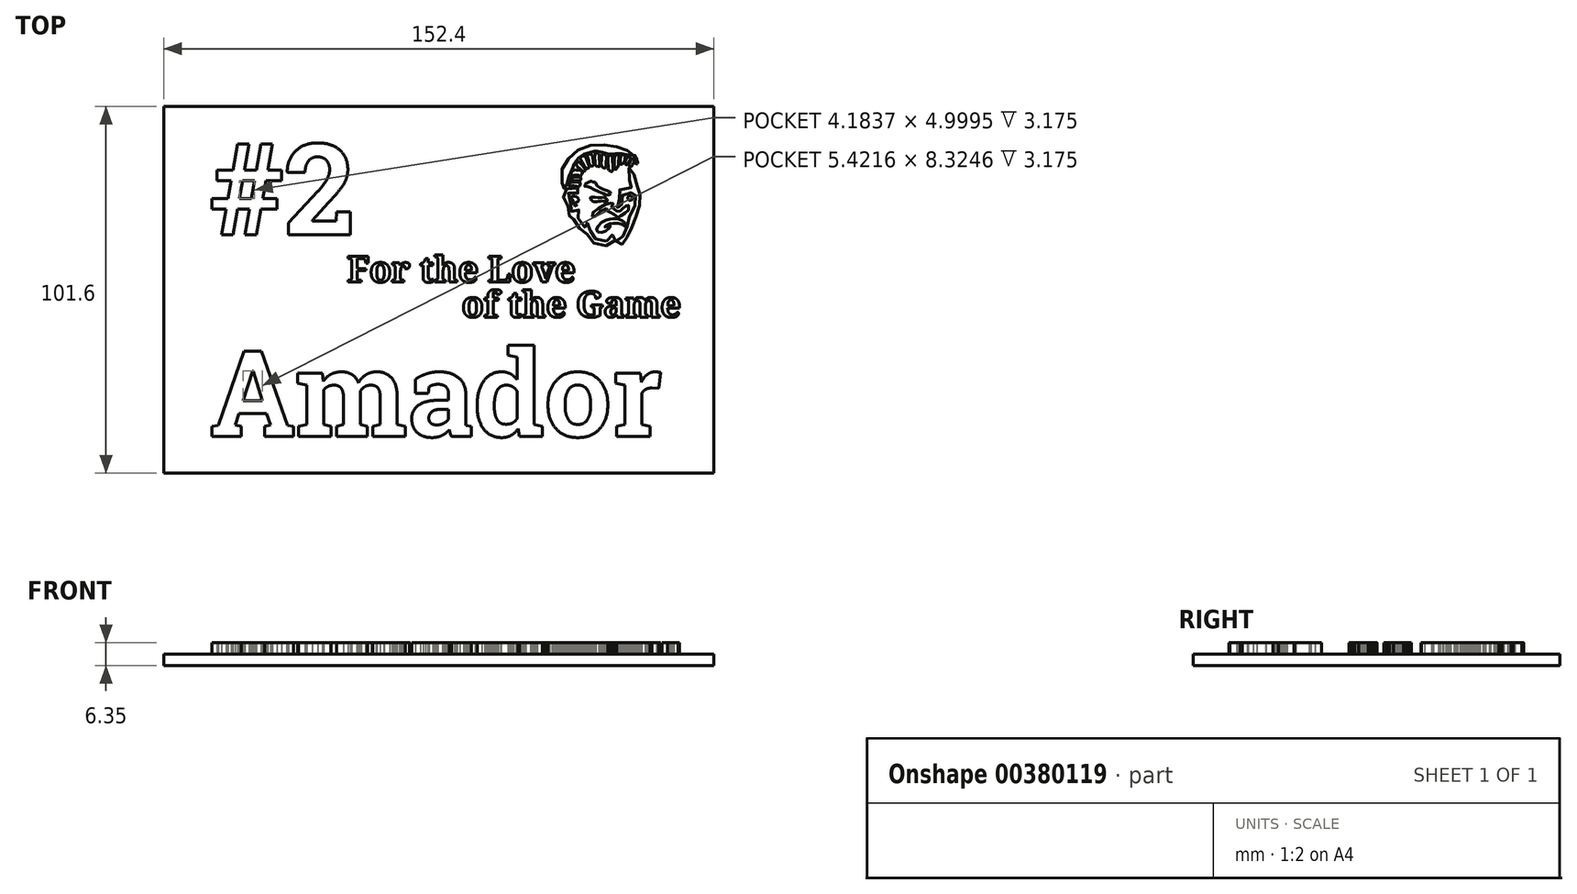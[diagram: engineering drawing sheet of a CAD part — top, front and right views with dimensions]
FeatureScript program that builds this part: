
annotation { "Feature Type Name" : "Feature", "Feature Type Description" : "" }
export const myFeature = defineFeature(function(context is Context, id is Id, definition is map)
    precondition{}
    {
        {
            var Q0;
            Q0=qCreatedBy(makeId("Top.planeOp"),FACE);
            var sketch = newSketch(context, id + "F0", { "sketchPlane" : qUnion([Q0])});
            skLineSegment(sketch, "E0.bottom", {"start": v(-75.13, 26) * mm, "end": v(77.27, 26) * mm});
            skLineSegment(sketch, "E0.top", {"start": v(-75.13, -75.6) * mm, "end": v(77.27, -75.6) * mm});
            skLineSegment(sketch, "E0.left", {"start": v(-75.13, 26) * mm, "end": v(-75.13, -75.6) * mm});
            skLineSegment(sketch, "E0.right", {"start": v(77.27, 26) * mm, "end": v(77.27, -75.6) * mm});
            skSolve(sketch);
        }
        {
            var Q0;
            Q0=makeQuery(id+"F0.imprint","IMPRINT",FACE,{"disambiguationData":[TD([[makeQuery(id+"F0.imprint","IMPRINT",EDGE,{"derivedFrom":sQuery(id+"F0.wireOp",EDGE,"E0.bottom")}),-1.0]])]});
            var sketch = newSketch(context, id + "F1", { "sketchPlane" : qUnion([Q0])});
            skFitSpline(sketch, "E1", {"points": [v(47.57, -11.3) * mm, v(48.35, -11.04) * mm, v(48.7, -10.35) * mm, v(49.04, -9.7) * mm, v(49.57, -9.46) * mm, v(50.02, -9.78) * mm, v(50.06, -10.58) * mm, v(49.74, -11.5) * mm, v(49.1, -12.15) * mm, v(47.63, -12.55) * mm, v(46.12, -12.5) * mm, v(44.61, -12.12) * mm, v(43.38, -11.34) * mm, v(42.6, -10.32) * mm, v(42.24, -9.52) * mm, v(42.15, -9.31) * mm, v(41.34, -8.82) * mm, v(40.33, -8.02) * mm, v(39.44, -7.2) * mm, v(38.67, -6.1) * mm, v(38.42, -5) * mm, v(38.42, -4.22) * mm, v(38.35, -4.2) * mm, v(37.68, -4.39) * mm, v(37.16, -4.27) * mm, v(36.95, -3.72) * mm, v(36.86, -2.5) * mm, v(36.8, -1.48) * mm, v(36.67, -1.07) * mm, v(35.77, 0.2) * mm, v(35.58, 1.07) * mm, v(35.86, 2.13) * mm, v(36.18, 2.7) * mm, v(36.53, 3.12) * mm, v(37.23, 3.22) * mm, v(39.03, 3.4) * mm, v(39.82, 3.34) * mm, v(40.19, 3.09) * mm, v(40.23, 2.45) * mm, v(39.66, 1.98) * mm, v(38.93, 1.9) * mm, v(38.59, 2.03) * mm, v(37.24, 2.03) * mm, v(36.72, 1.65) * mm, v(36.72, 0.85) * mm, v(37.32, -0.2) * mm, v(37.77, -1.18) * mm, v(37.85, -2.09) * mm, v(37.9, -3.1) * mm, v(37.99, -3.1) * mm, v(38.63, -3.1) * mm, v(39.4, -2.76) * mm, v(39.72, -2.59) * mm, v(39.8, -2.7) * mm, v(39.73, -3.22) * mm, v(39.6, -4) * mm, v(39.6, -4.77) * mm, v(40.1, -5.82) * mm, v(41.16, -7.15) * mm, v(41.6, -7.53) * mm, v(41.9, -7.56) * mm, v(41.89, -7.44) * mm, v(41.82, -6.61) * mm, v(42, -6.23) * mm, v(42.5, -6.3) * mm, v(42.8, -6.61) * mm, v(43.05, -7.98) * mm, v(43.22, -8.82) * mm, v(43.51, -9.54) * mm, v(44.12, -10.4) * mm, v(45.11, -11.01) * mm, v(46.32, -11.33) * mm, v(47.57, -11.3) * mm]});
            skFitSpline(sketch, "E2", {"points": [v(47.8, -7.3) * mm, v(47.13, -7.42) * mm, v(47.01, -7.42) * mm, v(47.13, -7.18) * mm, v(48.11, -6.65) * mm, v(49.11, -6.46) * mm, v(50.54, -6.45) * mm, v(51.76, -6.67) * mm, v(52.61, -7.21) * mm, v(52.82, -7.33) * mm, v(52.97, -7.12) * mm, v(52.7, -6.5) * mm, v(52.11, -5.74) * mm, v(50.6, -5.18) * mm, v(49.08, -5.16) * mm, v(48.46, -5.24) * mm, v(47.16, -5.6) * mm, v(45.65, -6.61) * mm, v(44.86, -7.78) * mm, v(44.9, -8.5) * mm, v(45.47, -8.94) * mm, v(46.7, -8.8) * mm, v(47.75, -8.16) * mm, v(48.56, -7.4) * mm, v(48.6, -7.12) * mm, v(47.8, -7.3) * mm]});
            skFitSpline(sketch, "E3", {"points": [v(51.85, -12.22) * mm, v(51.05, -12.44) * mm, v(50.33, -12.28) * mm, v(50.13, -11.73) * mm, v(50.52, -11.04) * mm, v(51.15, -10.86) * mm, v(51.76, -10.57) * mm, v(52.13, -10) * mm, v(52.3, -9.2) * mm, v(52.67, -8.25) * mm, v(53.2, -7.5) * mm, v(53.55, -6.76) * mm, v(53.63, -5.82) * mm, v(53.78, -4.85) * mm, v(54.49, -3.73) * mm, v(55.3, -2.73) * mm, v(55.42, -1.6) * mm, v(55.17, -0.4) * mm, v(55.2, 0.11) * mm, v(55.52, 1.32) * mm, v(55.57, 2.16) * mm, v(55.47, 2.42) * mm, v(54.99, 2.38) * mm, v(54.56, 2.14) * mm, v(53.7, 2.1) * mm, v(52.55, 2.06) * mm, v(52.07, 1.77) * mm, v(51.98, 1.02) * mm, v(52.2, 0.28) * mm, v(52.08, -0.6) * mm, v(51.72, -1.24) * mm, v(51.47, -1.75) * mm, v(51.5, -2.22) * mm, v(51.32, -2.4) * mm, v(50.6, -2.13) * mm, v(50.38, -1.6) * mm, v(50.64, -0.97) * mm, v(51, -0.17) * mm, v(51.06, 0.44) * mm, v(50.78, 1.07) * mm, v(50.66, 1.97) * mm, v(51.18, 2.9) * mm, v(52.12, 3.24) * mm, v(53.3, 3.36) * mm, v(54.52, 3.48) * mm, v(54.66, 3.6) * mm, v(54.38, 3.97) * mm, v(54, 4.8) * mm, v(53.79, 6.28) * mm, v(53.9, 7.94) * mm, v(53.79, 8.9) * mm, v(53.79, 9.1) * mm, v(54.03, 9.04) * mm, v(54.76, 8.52) * mm, v(55.13, 7.38) * mm, v(55.34, 5.97) * mm, v(55.56, 4.72) * mm, v(56.14, 3.87) * mm, v(56.71, 3.56) * mm, v(57.08, 2.91) * mm, v(56.95, 1.93) * mm, v(56.51, 0.55) * mm, v(56.4, -0.31) * mm, v(56.62, -1.36) * mm, v(56.69, -2.19) * mm, v(56.32, -3.56) * mm, v(55.4, -4.86) * mm, v(54.62, -5.8) * mm, v(54.5, -7.08) * mm, v(54.37, -8.24) * mm, v(53.76, -9.26) * mm, v(53.43, -9.82) * mm, v(53.28, -10.59) * mm, v(53.14, -11.27) * mm, v(52.34, -11.95) * mm, v(51.85, -12.22) * mm]});
            skFitSpline(sketch, "E4", {"points": [v(51.65, -4.28) * mm, v(52.13, -3.81) * mm, v(53.02, -3.37) * mm, v(53.66, -2.72) * mm, v(53.77, -1.9) * mm, v(53.38, -1.13) * mm, v(53.21, -1.15) * mm, v(53, -1.68) * mm, v(52.43, -2.14) * mm, v(51.8, -2.46) * mm, v(51.42, -2.92) * mm, v(50.93, -3.27) * mm, v(50.6, -3.17) * mm, v(50.13, -2.68) * mm, v(49.7, -2.46) * mm, v(49.28, -2.45) * mm, v(49, -1.98) * mm, v(49.06, -1.41) * mm, v(49.39, -0.94) * mm, v(49.4, -0.71) * mm, v(48.82, -0.74) * mm, v(47.56, -0.99) * mm, v(45.6, -2.02) * mm, v(44.06, -3.24) * mm, v(43.57, -3.77) * mm, v(43.7, -4.86) * mm, v(43.9, -4.88) * mm, v(44.45, -4.27) * mm, v(46.1, -2.93) * mm, v(47.41, -2.3) * mm, v(47.63, -2.3) * mm, v(47.73, -2.85) * mm, v(48.15, -3.33) * mm, v(48.9, -3.44) * mm, v(49.24, -3.55) * mm, v(49.84, -4.18) * mm, v(50.54, -4.68) * mm, v(51.18, -4.66) * mm, v(51.65, -4.28) * mm]});
            skFitSpline(sketch, "E5", {"points": [v(54.73, 0.39) * mm, v(54.77, 0.82) * mm, v(54.18, 1.2) * mm, v(53.55, 1.02) * mm, v(53.47, 0.3) * mm, v(54.02, 0) * mm, v(54.73, 0.39) * mm]});
            skFitSpline(sketch, "E6", {"points": [v(44.44, -0.47) * mm, v(43.66, -0.25) * mm, v(43.08, 0.44) * mm, v(43.14, 0.75) * mm, v(43.78, 0.8) * mm, v(46.74, 0.78) * mm, v(47.17, 0.7) * mm, v(47.78, -0.13) * mm, v(47.64, -0.32) * mm, v(46.64, -0.26) * mm, v(45.29, -0.32) * mm, v(44.44, -0.47) * mm]});
            skFitSpline(sketch, "E7", {"points": [v(46.65, 1.86) * mm, v(47.46, 1.48) * mm, v(48.33, 1.53) * mm, v(48.69, 2.02) * mm, v(48.54, 2.32) * mm, v(47.26, 2.83) * mm, v(45.32, 3.72) * mm, v(44.79, 4.23) * mm, v(44.53, 4.83) * mm, v(44.13, 5) * mm, v(43.88, 5) * mm, v(43.34, 5.26) * mm, v(43.09, 5.3) * mm, v(42.9, 5.05) * mm, v(42.6, 5.07) * mm, v(42.3, 4.85) * mm, v(42.2, 4.73) * mm, v(41.9, 4.72) * mm, v(41.8, 4.5) * mm, v(41.38, 4.05) * mm, v(41.56, 3.84) * mm, v(42.59, 3.74) * mm, v(43.78, 3.19) * mm, v(46.65, 1.86) * mm]});
            skFitSpline(sketch, "E8", {"points": [v(39.09, -1.2) * mm, v(38.85, -1.02) * mm, v(39.04, -0.63) * mm, v(39.6, -0.4) * mm, v(39.72, 0.33) * mm, v(39.01, 1.06) * mm, v(38.23, 1.1) * mm, v(37.7, 0.65) * mm, v(37.83, 0.29) * mm, v(38.12, 0.15) * mm, v(38.31, -0.34) * mm, v(38.52, -1.23) * mm, v(38.92, -1.63) * mm, v(39.18, -1.51) * mm, v(39.26, -1.2) * mm, v(39.09, -1.2) * mm]});
            skFitSpline(sketch, "E9", {"points": [v(35.18, 4.73) * mm, v(35.4, 3.4) * mm, v(35.76, 3.05) * mm, v(35.87, 3.13) * mm, v(36.08, 3.42) * mm, v(36.43, 3.67) * mm, v(36.66, 4.42) * mm, v(36.6, 5.36) * mm, v(37.02, 6.1) * mm, v(37.15, 6.7) * mm, v(37.23, 7.46) * mm, v(37.88, 8.4) * mm, v(38.45, 9.02) * mm, v(38.56, 9.75) * mm, v(38.74, 10.4) * mm, v(39.17, 10.98) * mm, v(39.64, 11.29) * mm, v(39.78, 11.9) * mm, v(40.12, 12.28) * mm, v(40.85, 12.68) * mm, v(41.65, 12.77) * mm, v(42.03, 12.99) * mm, v(42.91, 13.25) * mm, v(43.49, 13.17) * mm, v(43.91, 13.25) * mm, v(44.22, 13.54) * mm, v(44.87, 13.6) * mm, v(45.62, 13.32) * mm, v(46.3, 13.31) * mm, v(46.91, 13.3) * mm, v(47.51, 12.81) * mm, v(48.11, 12.71) * mm, v(48.8, 12.83) * mm, v(49.39, 12.68) * mm, v(50.13, 12.89) * mm, v(50.83, 12.96) * mm, v(51.35, 12.83) * mm, v(51.87, 12.94) * mm, v(52.53, 12.95) * mm, v(53.18, 12.6) * mm, v(53.93, 12.6) * mm, v(54.48, 12.4) * mm, v(54.65, 12.18) * mm, v(55.03, 12.55) * mm, v(54.73, 12.89) * mm, v(53.9, 13.45) * mm, v(51.53, 14.51) * mm, v(50.44, 14.76) * mm, v(49.1, 15.08) * mm, v(45.83, 15.4) * mm, v(43.17, 15.22) * mm, v(40.97, 14.54) * mm, v(38.6, 13.18) * mm, v(36.98, 11.4) * mm, v(35.34, 9.1) * mm, v(35.2, 8.1) * mm, v(35.18, 4.73) * mm]});
            skFitSpline(sketch, "E10", {"points": [v(39.4, 5) * mm, v(39.96, 4.99) * mm, v(40.23, 4.82) * mm, v(40.1, 4) * mm, v(39.64, 3.78) * mm, v(38.94, 3.9) * mm, v(37.89, 3.94) * mm, v(37.45, 3.8) * mm, v(37.1, 4.04) * mm, v(37.54, 4.84) * mm, v(38.3, 5) * mm, v(39.4, 5) * mm]});
            skFitSpline(sketch, "E11", {"points": [v(37.48, 5.07) * mm, v(37.11, 4.96) * mm, v(36.94, 5.2) * mm, v(37.34, 5.9) * mm, v(37.75, 6.14) * mm, v(39.96, 6.47) * mm, v(40.35, 6.2) * mm, v(40.47, 5.65) * mm, v(40.11, 5.36) * mm, v(39.64, 5.4) * mm, v(38.37, 5.41) * mm, v(37.48, 5.07) * mm]});
            skFitSpline(sketch, "E12", {"points": [v(38.14, 6.82) * mm, v(39.68, 6.88) * mm, v(40, 6.74) * mm, v(40.54, 7) * mm, v(40.85, 7.85) * mm, v(40.67, 8.1) * mm, v(39.1, 8.4) * mm, v(38.41, 8.3) * mm, v(37.9, 7.73) * mm, v(37.48, 6.86) * mm, v(37.68, 6.74) * mm, v(38.14, 6.82) * mm]});
            skFitSpline(sketch, "E13", {"points": [v(39.26, 9.59) * mm, v(41, 8.1) * mm, v(41.32, 7.94) * mm, v(41.68, 8.33) * mm, v(41.53, 8.74) * mm, v(40.44, 10.1) * mm, v(39.87, 10.6) * mm, v(39.5, 10.56) * mm, v(39.13, 10.09) * mm, v(39.26, 9.59) * mm]});
            skFitSpline(sketch, "E14", {"points": [v(40.75, 10.65) * mm, v(40.33, 11.47) * mm, v(40.46, 11.98) * mm, v(41.21, 12.34) * mm, v(41.77, 12.07) * mm, v(42.13, 11.12) * mm, v(42.72, 9.33) * mm, v(42.65, 8.96) * mm, v(42.12, 8.81) * mm, v(41.62, 9.07) * mm, v(40.75, 10.65) * mm]});
            skFitSpline(sketch, "E15", {"points": [v(42.43, 11.4) * mm, v(42.21, 12.24) * mm, v(42.3, 12.64) * mm, v(43, 12.81) * mm, v(43.54, 12.53) * mm, v(43.83, 11.13) * mm, v(44, 9.88) * mm, v(43.65, 9.47) * mm, v(42.94, 9.8) * mm, v(42.43, 11.4) * mm]});
            skFitSpline(sketch, "E16", {"points": [v(44.29, 12.06) * mm, v(44.36, 12.96) * mm, v(44.5, 13.26) * mm, v(44.93, 13.17) * mm, v(45.54, 12.55) * mm, v(45.55, 11.97) * mm, v(45.6, 9.45) * mm, v(45.5, 9.32) * mm, v(44.61, 9.6) * mm, v(44.4, 10.08) * mm, v(44.29, 12.06) * mm]});
            skFitSpline(sketch, "E17", {"points": [v(46.05, 10.51) * mm, v(46.15, 9.53) * mm, v(46.62, 9.04) * mm, v(47.1, 8.88) * mm, v(47.3, 9.08) * mm, v(47.48, 10.9) * mm, v(47.53, 12.07) * mm, v(47.34, 12.46) * mm, v(46.68, 12.84) * mm, v(46.32, 12.79) * mm, v(46.17, 11.97) * mm, v(46.05, 10.51) * mm]});
            skFitSpline(sketch, "E18", {"points": [v(48.03, 8.99) * mm, v(48.11, 8.48) * mm, v(48.48, 8.11) * mm, v(48.94, 7.92) * mm, v(49.21, 8.2) * mm, v(49.24, 10.23) * mm, v(49.16, 12.1) * mm, v(48.83, 12.47) * mm, v(48.44, 12.47) * mm, v(47.98, 12) * mm, v(47.93, 10.87) * mm, v(48.03, 8.99) * mm]});
            skFitSpline(sketch, "E19", {"points": [v(49.71, 9.45) * mm, v(49.86, 8.66) * mm, v(50.13, 8.48) * mm, v(50.3, 8.75) * mm, v(50.76, 9.43) * mm, v(50.85, 10.13) * mm, v(50.93, 12.16) * mm, v(50.81, 12.6) * mm, v(50.31, 12.66) * mm, v(49.83, 12.22) * mm, v(49.7, 11.19) * mm, v(49.71, 9.45) * mm]});
            skFitSpline(sketch, "E20", {"points": [v(51.32, 10.54) * mm, v(51.4, 11.84) * mm, v(51.7, 12.52) * mm, v(52.3, 12.55) * mm, v(52.72, 12.21) * mm, v(52.63, 11.54) * mm, v(52.29, 10.26) * mm, v(51.93, 10.06) * mm, v(51.44, 9.99) * mm, v(51.32, 10.54) * mm]});
            skFitSpline(sketch, "E21", {"points": [v(52.63, 10.38) * mm, v(52.83, 11.01) * mm, v(53.35, 11.9) * mm, v(53.66, 12.08) * mm, v(54.13, 11.71) * mm, v(53.9, 10.95) * mm, v(53.35, 10.1) * mm, v(53.17, 9.86) * mm, v(52.8, 9.99) * mm, v(52.63, 10.38) * mm]});
            skFitSpline(sketch, "E22", {"points": [v(53.86, 10.18) * mm, v(53.7, 9.9) * mm, v(53.81, 9.57) * mm, v(54.15, 9.28) * mm, v(54.42, 9.39) * mm, v(55.14, 10.6) * mm, v(55.26, 11.14) * mm, v(55.02, 11.54) * mm, v(54.8, 11.61) * mm, v(54.48, 11.27) * mm, v(53.86, 10.18) * mm]});
            skFitSpline(sketch, "E23", {"points": [v(55.24, 11.7) * mm, v(55.54, 11.38) * mm, v(55.58, 10.83) * mm, v(55.47, 10.49) * mm, v(55.7, 10.04) * mm, v(55.92, 10.02) * mm, v(56.2, 10.63) * mm, v(56.05, 10.85) * mm, v(55.85, 11.61) * mm, v(55.63, 12) * mm, v(55.42, 12.46) * mm, v(55.15, 12.4) * mm, v(55.09, 11.93) * mm, v(55.24, 11.7) * mm]});
            skText(sketch, "E24", { "text": "For the Love", "fontName": "NotoSerif-Bold.ttf"});
            skText(sketch, "E25", { "text": "of the Game", "fontName": "NotoSerif-Bold.ttf"});
            skText(sketch, "E26", { "text": "#2", "fontName": "RobotoSlab-Bold.ttf"});
            skText(sketch, "E27", { "text": "Amador", "fontName": "RobotoSlab-Bold.ttf"});
            const initialGuessF1  = {"E24": [-0.02433, -0.0227, 1, 0, 0.00716], "E25": [0.00742, -0.0324, 1, 0, 0.00716], "E26": [-0.06243, -0.00956, 1, 0, 0.0254], "E27": [-0.06243, -0.06544, 1, 0, 0.02393]};
            skSetInitialGuess(sketch, initialGuessF1);
            skSolve(sketch);
        }
        {
            var Q0;
            Q0=qSketchRegion(id+"F0",true);
            extrude(context, id + "F2", {"entities" : qUnion([Q0]), "depth" : 3.17 * mm});
        }
        {
            var Q0;
            Q0=qSketchRegion(id+"F1",true);
            extrude(context, id + "F3", {"entities" : qUnion([Q0]), "operationType" : NewBodyOperationType.ADD, "depth" : 6.35 * mm});
        }
    });
